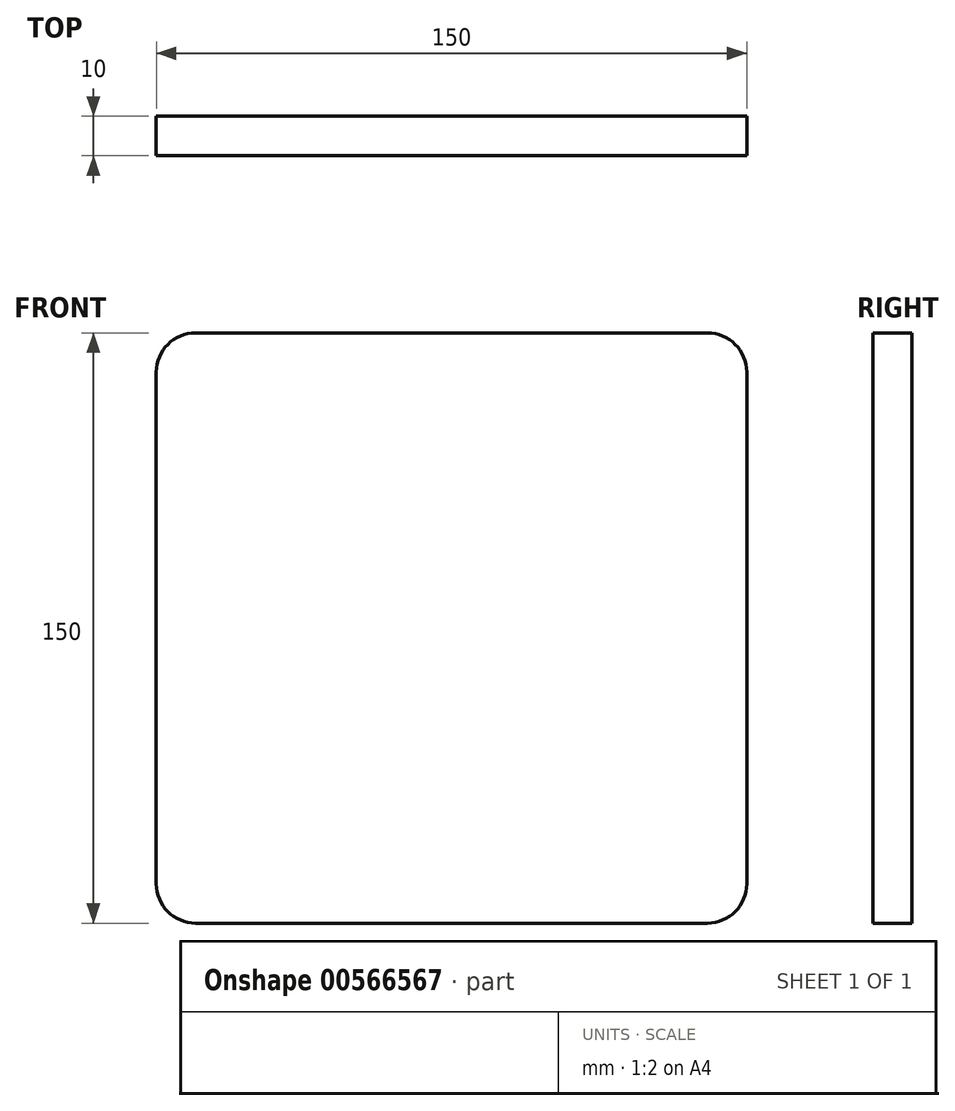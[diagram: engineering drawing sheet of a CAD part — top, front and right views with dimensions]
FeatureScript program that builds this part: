
annotation { "Feature Type Name" : "Feature", "Feature Type Description" : "" }
export const myFeature = defineFeature(function(context is Context, id is Id, definition is map)
    precondition{}
    {
        {
            var Q0;
            Q0=qCreatedBy(makeId("Front.planeOp"),FACE);
            var sketch = newSketch(context, id + "F0", { "sketchPlane" : qUnion([Q0])});
            skLineSegment(sketch, "E0.bottom", {"start": v(-50.4, 113.35) * mm, "end": v(99.6, 113.35) * mm});
            skLineSegment(sketch, "E0.top", {"start": v(-50.4, -36.65) * mm, "end": v(99.6, -36.65) * mm});
            skLineSegment(sketch, "E0.left", {"start": v(-50.4, 113.35) * mm, "end": v(-50.4, -36.65) * mm});
            skLineSegment(sketch, "E0.right", {"start": v(99.6, 113.35) * mm, "end": v(99.6, -36.65) * mm});
            skSolve(sketch);
        }
        {
            var Q0;
            Q0 = qSketchRegion(id + "F0", true);
            extrude(context, id + "F1", {"entities" : qUnion([Q0]), "depth" : 10 * mm, "offsetDistance" : 25 * mm});
        }
        {
            var Q0;
            Q0=makeQuery(id+"F1.opExtrude","SWEPT_EDGE",EDGE,{"disambiguationData":[OSD([sQuery(id+"F0.wireOp",EDGE,"E0.top"),sQuery(id+"F0.wireOp",EDGE,"E0.right")])]});
            fillet(context, id + "F2", {"entities" : qUnion([Q0]), "radius" : 10 * mm, "tangentPropagation" : true, "allowEdgeOverflow" : false});
        }
        {
            var Q0;
            Q0=makeQuery(id+"F1.opExtrude","SWEPT_EDGE",EDGE,{"disambiguationData":[OSD([sQuery(id+"F0.wireOp",EDGE,"E0.top"),sQuery(id+"F0.wireOp",EDGE,"E0.left")])]});
            fillet(context, id + "F3", {"entities" : qUnion([Q0]), "radius" : 10 * mm, "tangentPropagation" : true, "allowEdgeOverflow" : false});
        }
        {
            var Q0;
            Q0=makeQuery(id+"F1.opExtrude","SWEPT_EDGE",EDGE,{"disambiguationData":[OSD([sQuery(id+"F0.wireOp",EDGE,"E0.bottom"),sQuery(id+"F0.wireOp",EDGE,"E0.left")])]});
            fillet(context, id + "F4", {"entities" : qUnion([Q0]), "radius" : 10 * mm, "tangentPropagation" : true, "allowEdgeOverflow" : false});
        }
        {
            var Q0;
            Q0=makeQuery(id+"F1.opExtrude","SWEPT_EDGE",EDGE,{"disambiguationData":[OSD([sQuery(id+"F0.wireOp",EDGE,"E0.bottom"),sQuery(id+"F0.wireOp",EDGE,"E0.right")])]});
            fillet(context, id + "F5", {"entities" : qUnion([Q0]), "radius" : 10 * mm, "tangentPropagation" : true, "allowEdgeOverflow" : false});
        }
    });
